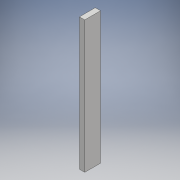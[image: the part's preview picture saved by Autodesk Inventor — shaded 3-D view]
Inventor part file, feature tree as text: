
AUTODESK INVENTOR PART (.ipt)
format: ipt  version: 2017 (Build 210142000, 142)  size: 91,136 bytes
history: native  units: mm
features: extrude x1, sketch x1
ambient origin geometry x8: Origin, YZ Plane, XZ Plane, XY Plane, X Axis, Y Axis, Z Axis, Center Point
bodies: Solid1 (feature_tree)
feature tree (2):
  extrude  "Extrusion1"  Depth=50.0mm
  sketch  "Sketch1"  dims[d0=6.0mm d1=50.0mm d2=2.0mm d3=0.0mm]
